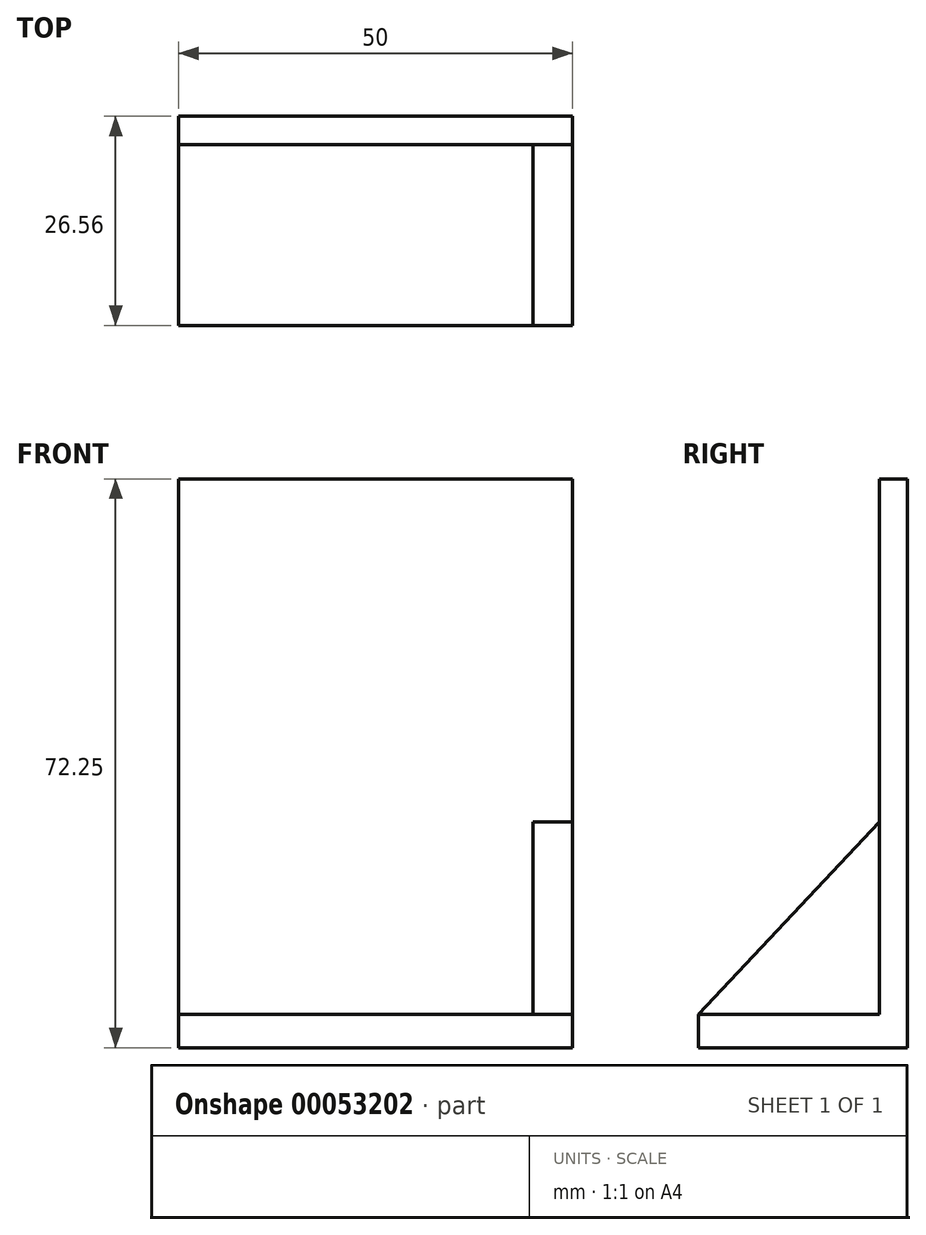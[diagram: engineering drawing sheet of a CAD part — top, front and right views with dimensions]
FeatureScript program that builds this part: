
annotation { "Feature Type Name" : "Feature", "Feature Type Description" : "" }
export const myFeature = defineFeature(function(context is Context, id is Id, definition is map)
    precondition{}
    {
        {
            var Q0;
            Q0=qCreatedBy(makeId("Right.planeOp"),FACE);
            var sketch = newSketch(context, id + "F0", { "sketchPlane" : qUnion([Q0])});
            skLineSegment(sketch, "E0", {"start": v(0, 43.58) * mm, "end": v(3.56, 43.58) * mm});
            skLineSegment(sketch, "E1", {"start": v(3.56, 43.58) * mm, "end": v(3.56, -28.67) * mm});
            skLineSegment(sketch, "E2", {"start": v(3.56, -28.67) * mm, "end": v(-23, -28.67) * mm});
            skLineSegment(sketch, "E3", {"start": v(-23, -28.67) * mm, "end": v(-23, -24.46) * mm});
            skLineSegment(sketch, "E4", {"start": v(-23, -24.46) * mm, "end": v(0, -24.46) * mm});
            skLineSegment(sketch, "E5", {"start": v(0, -24.46) * mm, "end": v(0, 43.58) * mm});
            skSolve(sketch);
        }
        {
            var Q0;
            Q0=makeQuery(id+"F0.imprint","IMPRINT",FACE,{"disambiguationData":[TD([[makeQuery(id+"F0.imprint","IMPRINT",EDGE,{"derivedFrom":sQuery(id+"F0.wireOp",EDGE,"E0")}),-1.0]])]});
            extrude(context, id + "F1", {"entities" : qUnion([Q0]), "depth" : 50 * mm});
        }
        {
            var Q0;
            Q0=makeQuery(id+"F1.opExtrude","CAP_FACE",FACE,{"disambiguationData":[OSD([sQuery(id+"F0.wireOp",EDGE,"E0"),sQuery(id+"F0.wireOp",EDGE,"E1"),sQuery(id+"F0.wireOp",EDGE,"E2"),sQuery(id+"F0.wireOp",EDGE,"E3"),sQuery(id+"F0.wireOp",EDGE,"E4"),sQuery(id+"F0.wireOp",EDGE,"E5")])],"isStart":false});
            var sketch = newSketch(context, id + "F2", { "sketchPlane" : qUnion([Q0])});
            skLineSegment(sketch, "E6", {"start": v(0, 0) * mm, "end": v(-23, -24.46) * mm});
            skLineSegment(sketch, "E7", {"start": v(-23, -24.46) * mm, "end": v(0, -24.46) * mm});
            skLineSegment(sketch, "E8", {"start": v(0, -24.46) * mm, "end": v(0, 0) * mm});
            skSolve(sketch);
        }
        {
            var Q0;
            Q0=makeQuery(id+"F2.imprint","IMPRINT",FACE,{"disambiguationData":[TD([[makeQuery(id+"F2.imprint","IMPRINT",EDGE,{"derivedFrom":sQuery(id+"F2.wireOp",EDGE,"E6")}),1.0]])]});
            extrude(context, id + "F3", {"entities" : qUnion([Q0]), "oppositeDirection" : true, "depth" : 5 * mm});
        }
    });
